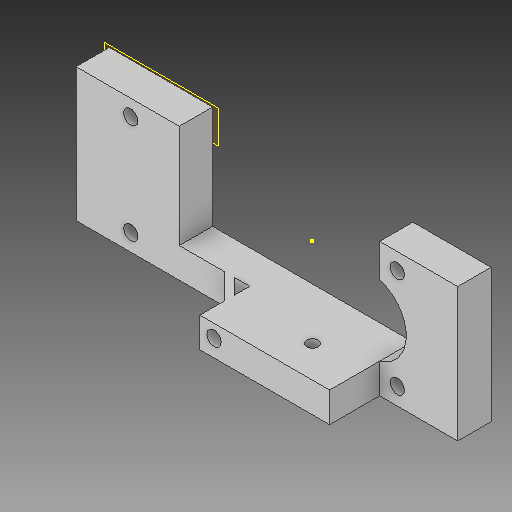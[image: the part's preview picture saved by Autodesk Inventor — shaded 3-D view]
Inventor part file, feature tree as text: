
AUTODESK INVENTOR PART (.ipt)
format: ipt  version: 2017 (Build 210142000, 142)  size: 171,520 bytes
history: native  units: mm
features: sketch x8, extrude x7, other x7, projected_geometry x2
ambient origin geometry x8: Origin, YZ Plane, XZ Plane, XY Plane, X Axis, Y Axis, Z Axis, Center Point
bodies: Solide1 (feature_tree)
feature tree (24):
  extrude  "Extrusion1"  Depth=10.0mm TaperAngle=0.0deg
  extrude  "Extrusion2"  Depth=15.0mm TaperAngle=0.0deg
  extrude  "Extrusion3"  Depth=31.0mm TaperAngle=0.0deg
  other  "Plan de construction1"
  sketch  "Esquisse4"
  extrude  "Extrusion4"  Depth=31.0mm TaperAngle=0.0deg
  extrude  "Extrusion5"  Depth=15.5mm
  extrude  "Extrusion6"  Depth=20.0mm
  extrude  "Extrusion7"  Depth=3.5mm
  sketch  "Esquisse1"
  other  "Référence1"
  sketch  "Esquisse2"
  projected_geometry  "Boucle projetée1"
  sketch  "Esquisse3"
  projected_geometry  "Boucle projetée2"
  sketch  "Esquisse5"
  other  "Référence2"
  sketch  "Esquisse6"
  sketch  "Esquisse7"
  sketch  "Esquisse8"
  other  "<userpath>\Documents\Modele 3D\Lanceur boule\Ensemble_Lanceur.iam"
  other  "Ensemble_Lanceur.iam"
  other  "support_arret:1"
  other  "lanceur:1"
